# Revit family: F052-28.25x36x32
name_source: partatom
category: Furniture Systems
units: mm (PartAtom-declared; Revit-internal decimal feet)

## family parameters
Always vertical = Yes
Cut with Voids When Loaded = No
Part Type = Normal
Room Calculation Point = No
Round Connector Dimension = Use Diameter
Shared = No
Work Plane-Based = No

## types (5) — shared parameters
6" Rectangle Leg = <By Category>
Base = <By Category>
Caster = Default New Material(1)
Chair Fabric = <By Category>
Description = Social Series - Right Social Chair (Seat height 18")
LEG H = 0' - 6 3/4"
Manufacturer = FOMCORE
Mod Leg = <By Category>
Model = F052-28.25x36x32
Pillow Fabric = <By Category>
Sled Leg 29 = <By Category>
Triangle Leg = <By Category>
URL = https://fomcore.com

## per-type parameters (varying)
| type | C6 | LEG OPTIONS | M6 | R6 | S29 | T6 |
| F052-28.25x36x32-C6 | Yes | 1 | No | No | No | No |
| F052-28.25x36x32-M6 | No | 2 | Yes | No | No | No |
| F052-28.25x36x32-R6 | No | 3 | No | Yes | No | No |
| F052-28.25x36x32-S29 | No | 4 | No | No | Yes | No |
| F052-28.25x36x32-T6 | No | 5 | No | No | No | Yes |

## geometry (parser evidence)
native form markers: Sweep x2
no freeform markers — native parametric forms only
